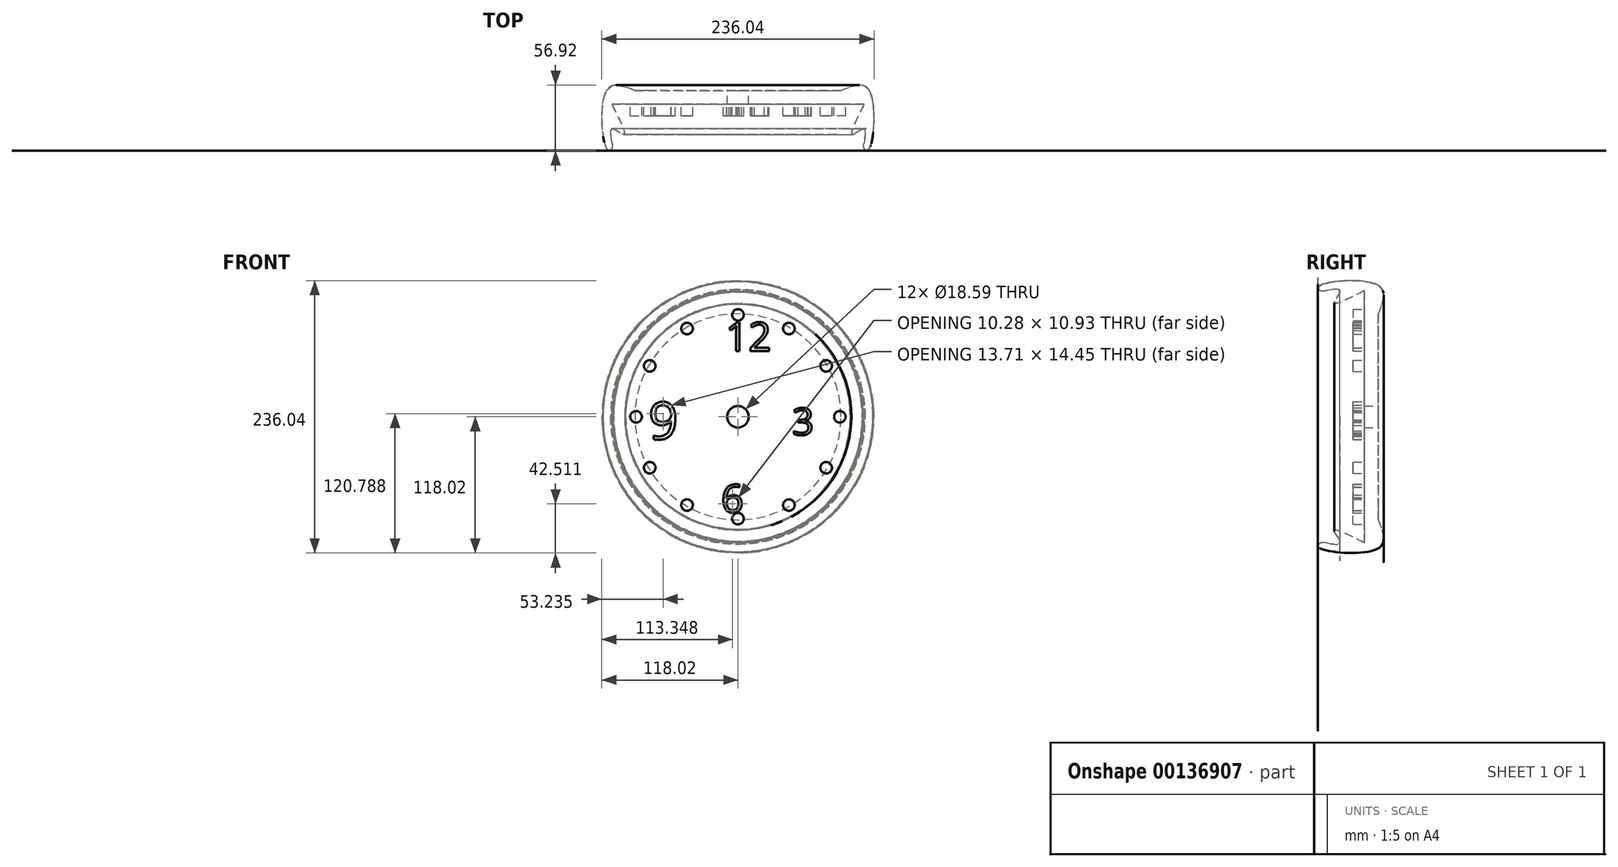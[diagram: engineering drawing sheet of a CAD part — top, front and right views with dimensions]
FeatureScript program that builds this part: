
annotation { "Feature Type Name" : "Feature", "Feature Type Description" : "" }
export const myFeature = defineFeature(function(context is Context, id is Id, definition is map)
    precondition{}
    {
        {
            var Q0;
            Q0=qCreatedBy(makeId("Right.planeOp"),FACE);
            var sketch = newSketch(context, id + "F0", { "sketchPlane" : qUnion([Q0])});
            skLineSegment(sketch, "E0", {"start": v(0, 0) * mm, "end": v(-61.2, 0) * mm});
            skLineSegment(sketch, "E1", {"start": v(-24.72, 9.3) * mm, "end": v(-36.72, 9.3) * mm});
            skLineSegment(sketch, "E2", {"start": v(-36.72, 9.3) * mm, "end": v(-36.72, 109.3) * mm});
            skLineSegment(sketch, "E3", {"start": v(-24.72, 9.3) * mm, "end": v(-24.72, 89.3) * mm});
            skFitSpline(sketch, "E4", {"points": [v(-36.72, 109.3) * mm, v(-63.02, 99.06) * mm, v(-58.03, 109.3) * mm, v(-69.82, 109.3) * mm, v(-74.9, 109.3) * mm, v(-76.73, 112.8) * mm, v(-24.72, 113.92) * mm, v(-24.72, 89.3) * mm], "startDerivative": vector(-213.56, -107.8) * mm, "endDerivative": vector(-68.77, -170.14) * mm});
            skSolve(sketch);
        }
        {
            var Q0;
            Q0 = qSketchRegion(id + "F0", true);
            var Q1;
            Q1=sQuery(id+"F0.wireOp",EDGE,"E0");
            revolve(context, id + "F1", {"entities" : qUnion([Q0]), "axis" : qUnion([Q1]), "revolveType" : RevolveType.FULL});
        }
        {
            var Q0;
            Q0=makeQuery(id+"F1.opRevolve","SWEPT_FACE",FACE,{"disambiguationData":[OSD([sQuery(id+"F0.wireOp",EDGE,"E2")])]});
            var sketch = newSketch(context, id + "F2", { "sketchPlane" : qUnion([Q0])});
            skCircle(sketch, "E5", {"center": v(0, 88.3) * mm, "radius": 5 * mm});
            skSolve(sketch);
        }
        {
            var Q0;
            Q0 = qSketchRegion(id + "F2", true);
            extrude(context, id + "F3", {"entities" : qUnion([Q0]), "operationType" : NewBodyOperationType.ADD, "depth" : 10 * mm});
        }
        {
            var Q0;
            Q0=makeQuery(id+"F1.opRevolve","SWEPT_BODY",BODY,{"disambiguationData":[OSD([sQuery(id+"F0.wireOp",EDGE,"E1"),sQuery(id+"F0.wireOp",EDGE,"E2"),sQuery(id+"F0.wireOp",EDGE,"E3"),sQuery(id+"F0.wireOp",EDGE,"E4")])]});
            var Q1;
            Q1=makeQuery(id+"F1.opRevolve","SWEPT_EDGE",EDGE,{"disambiguationData":[OSD([sQuery(id+"F0.wireOp",EDGE,"E1"),sQuery(id+"F0.wireOp",EDGE,"E2")])]});
            circularPattern(context, id + "F4", {"entities" : qUnion([Q0]), "axis" : qUnion([Q1]), "angle" : 360 * degree, "instanceCount" : 12, "equalSpace" : true});
        }
        {
            var Q0;
            Q0=makeQuery(id+"F1.opRevolve","SWEPT_FACE",FACE,{"disambiguationData":[OSD([sQuery(id+"F0.wireOp",EDGE,"E2")])]});
            var sketch = newSketch(context, id + "F5", { "sketchPlane" : qUnion([Q0])});
            skText(sketch, "E6", { "text": "12", "fontName": "OpenSans-Regular.ttf"});
            skText(sketch, "E7", { "text": "3\n", "fontName": "OpenSans-Regular.ttf"});
            skText(sketch, "E8", { "text": "6\n", "fontName": "OpenSans-Regular.ttf"});
            skText(sketch, "E9", { "text": "9\n", "fontName": "OpenSans-Regular.ttf"});
            const initialGuessF5  = {"E6": [-0.01081, 0.05712, 1, 0, 0.02492], "E7": [0.04702, -0.01575, 1, 0, 0.0235], "E8": [-0.01457, -0.08298, 1, 0, 0.02445], "E9": [-0.07758, -0.01951, 1, 0, 0.03244]};
            skSetInitialGuess(sketch, initialGuessF5);
            skSolve(sketch);
        }
        {
            var Q0;
            Q0 = qSketchRegion(id + "F5", true);
            extrude(context, id + "F6", {"entities" : qUnion([Q0]), "depth" : 10 * mm});
        }
    });
